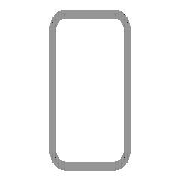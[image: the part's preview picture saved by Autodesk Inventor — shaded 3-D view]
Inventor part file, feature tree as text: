
AUTODESK INVENTOR PART (.ipt)
format: ipt  version: 2025 (Build 290162010, 162A)  size: 133,120 bytes
history: native  units: mm (DEFAULTED — no unit token found)
features: other x4, sketch x1, plane x1
ambient origin geometry x8: Origin, YZ Plane, XZ Plane, XY Plane, X Axis, Y Axis, Z Axis, Center Point
bodies: Solid1 (feature_tree), Body (feature_tree)
feature tree (6):
  parser-record x1  (decoder bookkeeping rows leaked as tree rows — omitted from the tree; the rows remain in map.json)
  other  "Driven Length"
  other  "Start Plane"
  other  "End Plane"
  sketch  "Sketch3"  dims[d3=840.0mm d4=0.0mm d7=6.0mm d9=40.0mm d11=60.0mm d12=3.0mm d13=-0.0mm d14=840.0mm d15=20.0mm d16=30.0mm d17=90.0deg d18=840.0mm]
  plane  "Work Plane3"
